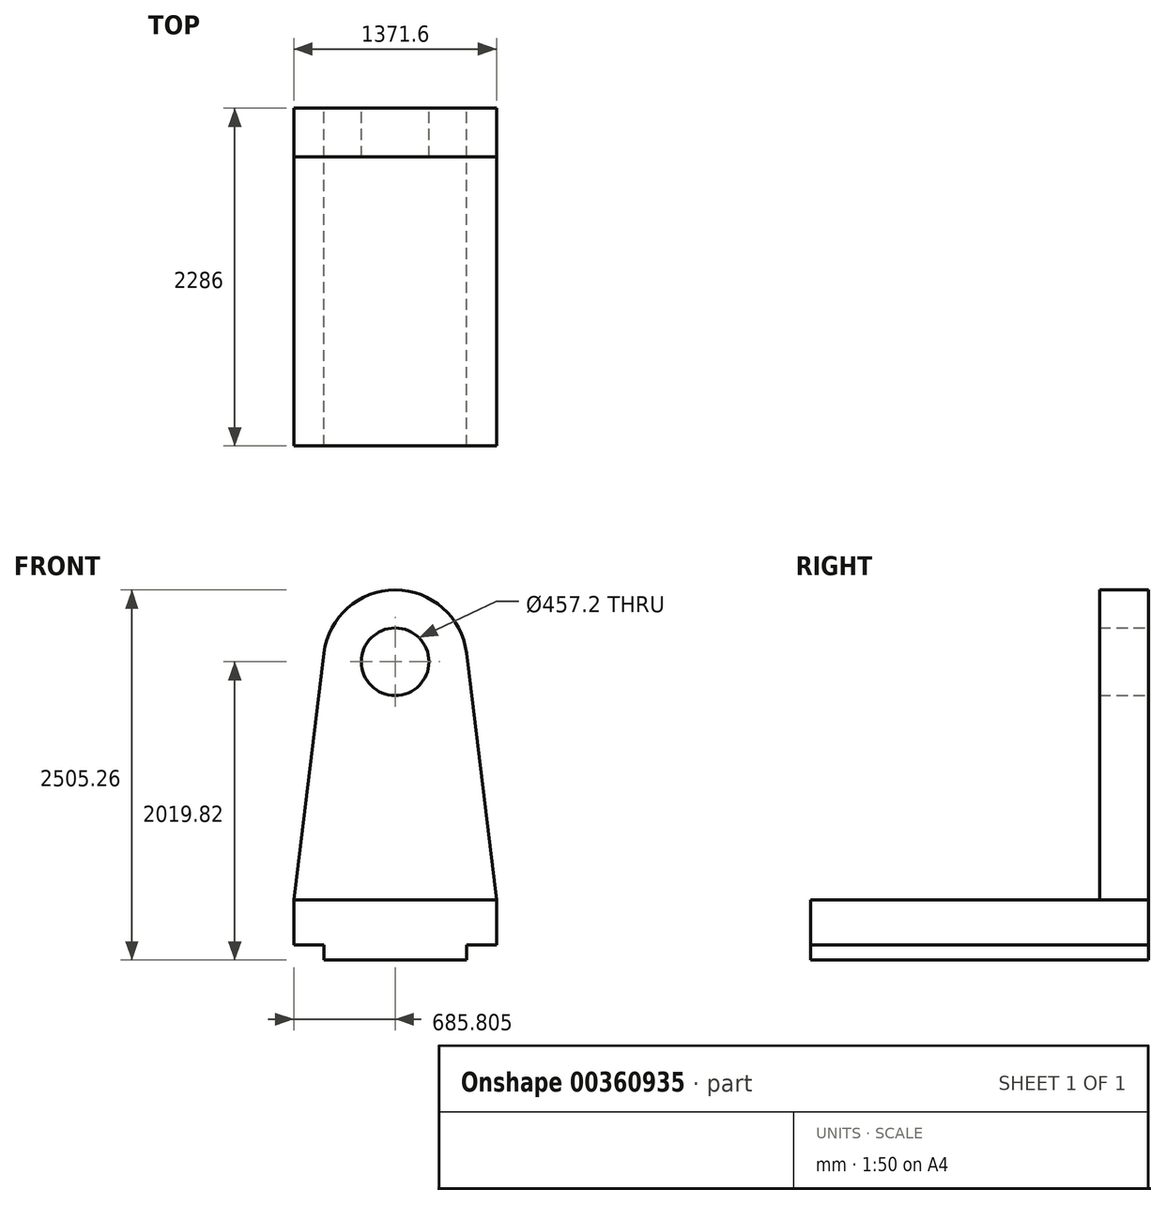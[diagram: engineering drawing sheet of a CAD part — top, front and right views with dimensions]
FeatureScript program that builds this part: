
annotation { "Feature Type Name" : "Feature", "Feature Type Description" : "" }
export const myFeature = defineFeature(function(context is Context, id is Id, definition is map)
    precondition{}
    {
        {
            var Q0;
            Q0=qCreatedBy(makeId("Front.planeOp"),FACE);
            var sketch = newSketch(context, id + "F0", { "sketchPlane" : qUnion([Q0])});
            skLineSegment(sketch, "E0", {"start": v(-405.42, -320.8) * mm, "end": v(559.78, -320.8) * mm});
            skLineSegment(sketch, "E1", {"start": v(559.78, -320.8) * mm, "end": v(559.78, -219.2) * mm});
            skLineSegment(sketch, "E2", {"start": v(559.78, -219.2) * mm, "end": v(762.98, -219.2) * mm});
            skLineSegment(sketch, "E3", {"start": v(762.98, -219.2) * mm, "end": v(762.98, 85.6) * mm});
            skLineSegment(sketch, "E4", {"start": v(762.98, 85.6) * mm, "end": v(-608.62, 85.6) * mm});
            skLineSegment(sketch, "E5", {"start": v(-608.62, 85.6) * mm, "end": v(-608.62, -219.2) * mm});
            skLineSegment(sketch, "E6", {"start": v(-608.62, -219.2) * mm, "end": v(-405.42, -219.2) * mm});
            skLineSegment(sketch, "E7", {"start": v(-405.42, -219.2) * mm, "end": v(-405.42, -320.8) * mm});
            skCircle(sketch, "E8", {"center": v(77.18, 1699.01) * mm, "radius": 228.6 * mm});
            skArc(sketch, "E9", {"start": v(559.05, 1757.78) * mm, "mid": v(77.18, 2184.45) * mm, "end": v(-404.68, 1757.78) * mm});
            skLineSegment(sketch, "E10", {"start": v(762.98, 85.6) * mm, "end": v(559.05, 1757.78) * mm});
            skLineSegment(sketch, "E11", {"start": v(-608.62, 85.6) * mm, "end": v(-404.68, 1757.78) * mm});
            skPoint(sketch, "E12.start.orphan", {"position": v(77.18, -320.8) * mm});
            skSolve(sketch);
        }
        {
            var Q0;
            Q0=makeQuery(id+"F0.imprint","IMPRINT",FACE,{"disambiguationData":[TD([[makeQuery(id+"F0.imprint","IMPRINT",EDGE,{"derivedFrom":sQuery(id+"F0.wireOp",EDGE,"E0")}),1.0]])]});
            extrude(context, id + "F1", {"entities" : qUnion([Q0]), "depth" : 2286 * mm});
        }
        {
            var Q0;
            Q0=makeQuery(id+"F0.imprint","IMPRINT",FACE,{"disambiguationData":[TD([[makeQuery(id+"F0.imprint","IMPRINT",EDGE,{"derivedFrom":sQuery(id+"F0.wireOp",EDGE,"E4")}),-1.0]])]});
            extrude(context, id + "F2", {"entities" : qUnion([Q0]), "operationType" : NewBodyOperationType.ADD, "depth" : 330.2 * mm});
        }
    });
